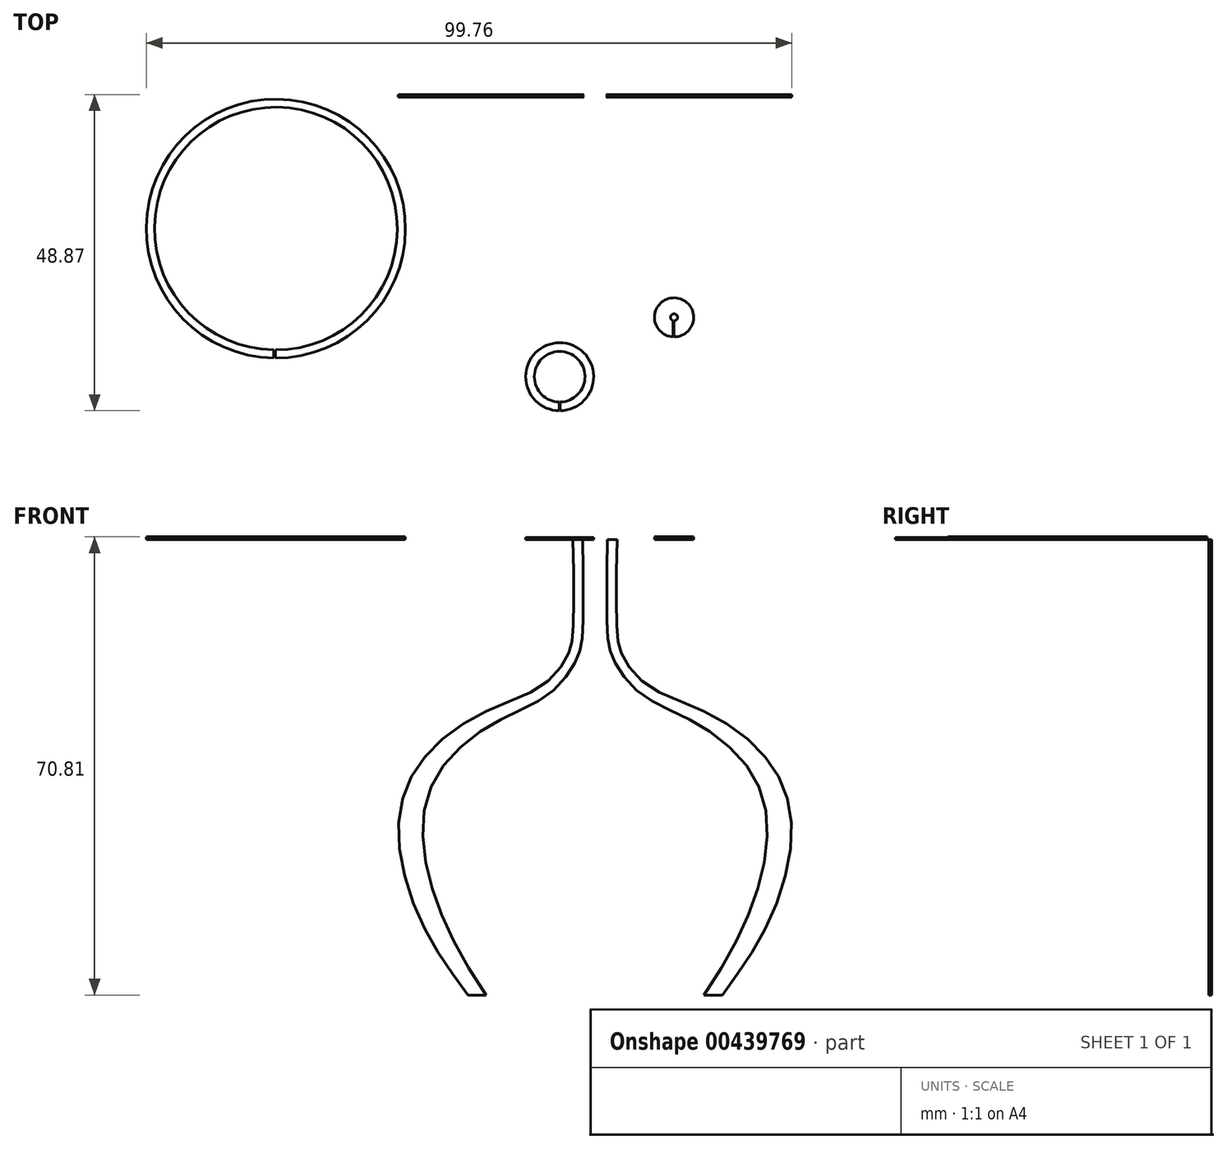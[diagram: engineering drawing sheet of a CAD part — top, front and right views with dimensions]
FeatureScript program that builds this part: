
annotation { "Feature Type Name" : "Feature", "Feature Type Description" : "" }
export const myFeature = defineFeature(function(context is Context, id is Id, definition is map)
    precondition{}
    {
        {
            var Q0;
            Q0=qCreatedBy(makeId("Front.planeOp"),FACE);
            var sketch = newSketch(context, id + "F0", { "sketchPlane" : qUnion([Q0])});
            skFitSpline(sketch, "E0", {"points": [v(1.88, 0) * mm, v(1.93, -14.64) * mm, v(2.8, -18.44) * mm, v(6.86, -23.7) * mm, v(15.33, -28.2) * mm, v(25.15, -37.75) * mm, v(25.57, -52.47) * mm, v(16.82, -70.41) * mm], "startDerivative": vector(0.15, -109.11) * mm, "endDerivative": vector(-67.3, -99) * mm});
            skLineSegment(sketch, "E1", {"start": v(1.88, 0) * mm, "end": v(3.42, 0) * mm});
            skLineSegment(sketch, "E2", {"start": v(16.82, -70.41) * mm, "end": v(19.65, -70.41) * mm});
            skFitSpline(sketch, "E3", {"points": [v(3.42, 0) * mm, v(3.42, -14.49) * mm, v(4.08, -17.6) * mm, v(7.76, -22.29) * mm, v(17.35, -26.78) * mm, v(26.94, -34.43) * mm, v(30.41, -44.74) * mm, v(26.84, -59.13) * mm, v(19.65, -70.41) * mm], "startDerivative": vector(-3.58, -116.19) * mm, "endDerivative": vector(-54.32, -73.83) * mm});
            skSolve(sketch);
        }
        {
            var Q0;
            Q0=makeQuery(id+"F0.imprint","IMPRINT",FACE,{"disambiguationData":[TD([[makeQuery(id+"F0.imprint","IMPRINT",EDGE,{"derivedFrom":sQuery(id+"F0.wireOp",EDGE,"E0")}),1.0]])]});
            extrude(context, id + "F1", {"entities" : qUnion([Q0]), "depth" : 0.4 * mm});
        }
        {
            var Q0;
            Q0=qCreatedBy(makeId("Top.planeOp"),FACE);
            var sketch = newSketch(context, id + "F2", { "sketchPlane" : qUnion([Q0])});
            skArc(sketch, "E4", {"start": v(-49.42, -40.73) * mm, "mid": v(-49.13, -0.69) * mm, "end": v(-49.65, -40.72) * mm});
            skArc(sketch, "E5", {"start": v(-49.42, -39.47) * mm, "mid": v(-49.13, -1.95) * mm, "end": v(-49.65, -39.46) * mm});
            skLineSegment(sketch, "E6", {"start": v(-49.65, -40.72) * mm, "end": v(-49.65, -39.46) * mm});
            skLineSegment(sketch, "E7", {"start": v(-49.42, -39.47) * mm, "end": v(-49.42, -40.73) * mm});
            skSolve(sketch);
        }
        {
            var Q0;
            Q0=makeQuery(id+"F2.imprint","IMPRINT",FACE,{"disambiguationData":[TD([[makeQuery(id+"F2.imprint","IMPRINT",EDGE,{"derivedFrom":sQuery(id+"F2.wireOp",EDGE,"E4")}),1.0]])]});
            extrude(context, id + "F3", {"entities" : qUnion([Q0]), "depth" : .4 * mm});
        }
        {
            var Q0;
            Q0=makeQuery(id+"F1.opExtrude","SWEPT_BODY",BODY,{"disambiguationData":[OSD([sQuery(id+"F0.wireOp",EDGE,"E0"),sQuery(id+"F0.wireOp",EDGE,"E1"),sQuery(id+"F0.wireOp",EDGE,"E2"),sQuery(id+"F0.wireOp",EDGE,"E3")])]});
            var Q1;
            Q1=qCreatedBy(makeId("Right.planeOp"),FACE);
            mirror(context, id + "F4", {"entities" : qUnion([Q0]), "mirrorPlane" : qUnion([Q1])});
        }
        {
            var Q0;
            Q0=qCreatedBy(makeId("Top.planeOp"),FACE);
            var sketch = newSketch(context, id + "F5", { "sketchPlane" : qUnion([Q0])});
            skArc(sketch, "E8", {"start": v(-5.38, -48.87) * mm, "mid": v(-5.48, -38.36) * mm, "end": v(-5.5, -48.87) * mm});
            skArc(sketch, "E9", {"start": v(-5.38, -47.52) * mm, "mid": v(-5.48, -39.7) * mm, "end": v(-5.5, -47.52) * mm});
            skLineSegment(sketch, "E10", {"start": v(-5.5, -48.87) * mm, "end": v(-5.5, -47.52) * mm});
            skLineSegment(sketch, "E11", {"start": v(-5.38, -48.87) * mm, "end": v(-5.38, -47.52) * mm});
            skSolve(sketch);
        }
        {
            var Q0;
            Q0 = qSketchRegion(id + "F5", true);
            extrude(context, id + "F6", {"entities" : qUnion([Q0]), "depth" : .3 * mm});
        }
        {
            var Q0;
            Q0=qCreatedBy(makeId("Top.planeOp"),FACE);
            var sketch = newSketch(context, id + "F7", { "sketchPlane" : qUnion([Q0])});
            skArc(sketch, "E12", {"start": v(12.19, -37.45) * mm, "mid": v(12.29, -31.4) * mm, "end": v(12.08, -37.45) * mm});
            skArc(sketch, "E13", {"start": v(12.19, -34.97) * mm, "mid": v(12.29, -33.9) * mm, "end": v(12.08, -34.95) * mm});
            skLineSegment(sketch, "E14", {"start": v(12.08, -37.45) * mm, "end": v(12.08, -34.95) * mm});
            skLineSegment(sketch, "E15", {"start": v(12.19, -37.45) * mm, "end": v(12.19, -34.95) * mm});
            skSolve(sketch);
        }
        {
            var Q0;
            Q0 = qSketchRegion(id + "F7", true);
            extrude(context, id + "F8", {"entities" : qUnion([Q0]), "depth" : .4 * mm});
        }
        {
            var Q0;
            Q0=makeQuery(id+"F2.imprint","IMPRINT",FACE,{"disambiguationData":[TD([[makeQuery(id+"F2.imprint","IMPRINT",EDGE,{"derivedFrom":sQuery(id+"F2.wireOp",EDGE,"E4")}),1.0]])]});
            extrude(context, id + "F9", {"entities" : qUnion([Q0]), "depth" : .4 * mm});
        }
    });
